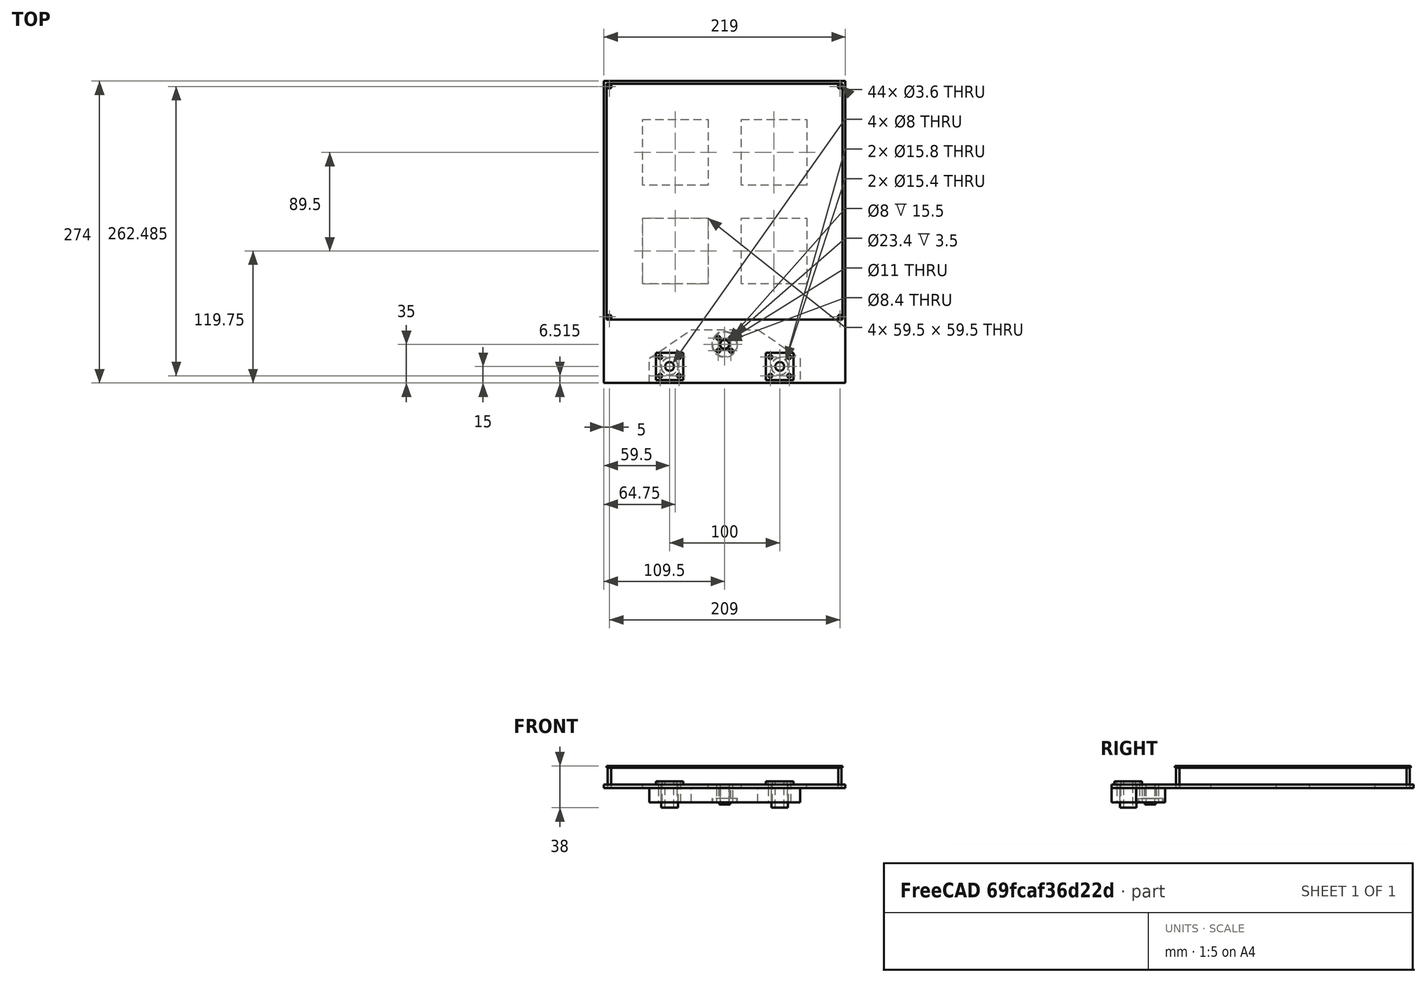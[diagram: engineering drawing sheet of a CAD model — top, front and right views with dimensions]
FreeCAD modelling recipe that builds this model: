
FCSTD DOCUMENT  (FreeCAD 0.16R6706 (Git))
Label: Montagem Mesa
License: All rights reserved
LicenseURL: http://en.wikipedia.org/wiki/All_rights_reserved
objects: Part::FeaturePython×6, Part::Cylinder×4, Part::Compound×1
note: 11 computed .brp shape members not serialized (recipe doc carries the construction recipe); baked Part::Feature solids carry a one-line shape summary decoded from their .brp

FEATURE [Part::FeaturePython] Suporte_Mesa_01  # a2plus imported part (geometry in sourceFile) (typed FeaturePython)
  Placement = pos=(0,-164.5,-18.4) rot=(0,0,1;0rad)
  fixedPosition = true
  sourceFile = <path> Mesa.FCStd
  timeLastImport = 1.50674e+09
  updateColors = true
FEATURE [Part::FeaturePython] Suporte_V_01  # a2plus imported part (geometry in sourceFile) (typed FeaturePython)
  Placement = pos=(0,-129.5,-31.4) rot=(0,0,1;0rad)
  fixedPosition = false
  sourceFile = <path> V.FCStd
  timeLastImport = 1.50665e+09
  updateColors = true
FEATURE [Part::FeaturePython] Castanha_TR8_01  # a2plus imported part (geometry in sourceFile) (typed FeaturePython)
  Placement = pos=(0,-129.5,-31.4) rot=(0,0,1;0rad)
  fixedPosition = false
  sourceFile = <path> TR8.FCStd
  timeLastImport = 1.50665e+09
  updateColors = true
FEATURE [Part::FeaturePython] LMK8UU_01  # a2plus imported part (geometry in sourceFile) (typed FeaturePython)
  Placement = pos=(-50,-149.5,-12.4) rot=(0.707107,0.707106,0;3.14159rad)
  fixedPosition = false
  sourceFile = <path>
  timeLastImport = 1.50665e+09
  updateColors = true
FEATURE [Part::FeaturePython] Mesa_MK1_01  # a2plus imported part (geometry in sourceFile) (typed FeaturePython)
  fixedPosition = false
  sourceFile = <path> MK1.FCStd
  timeLastImport = 1.50665e+09
  updateColors = true
FEATURE [Part::Cylinder] Cylinder  label="Regulador Mesa"
  Angle = 360
  Height = 20
  Placement = pos=(-104.5,104.5,-18.4) rot=(0,0,1;0rad)
  Radius = 1.5
FEATURE [Part::Cylinder] Cylinder001  label="Regulador Mesa001"
  Angle = 360
  Height = 20
  Placement = pos=(104.5,104.5,-18.4) rot=(0,0,1;0rad)
  Radius = 1.5
FEATURE [Part::Cylinder] Cylinder002  label="Regulador Mesa002"
  Angle = 360
  Height = 20
  Placement = pos=(104.5,-104.5,-18.4) rot=(0,0,1;0rad)
  Radius = 1.5
FEATURE [Part::Cylinder] Cylinder003  label="Regulador Mesa003"
  Angle = 360
  Height = 20
  Placement = pos=(-104.5,-104.5,-18.4) rot=(0,0,1;0rad)
  Radius = 1.5
FEATURE [Part::FeaturePython] LMK8UU_002  # a2plus imported part (geometry in sourceFile) (typed FeaturePython)
  Placement = pos=(50,-149.5,-12.4) rot=(0.707107,0.707107,0;3.14159rad)
  fixedPosition = false
  sourceFile = <path>
  timeLastImport = 1.50665e+09
  updateColors = true
FEATURE [Part::Compound] Compound
  Links = -> [LMK8UU_002,Cylinder003,Cylinder002,Cylinder001,Cylinder,Mesa_MK1_01,LMK8UU_01,Castanha_TR8_01,Suporte_V_01,Suporte_Mesa_01]
note: 6 file-system paths scrubbed to <path> (originals preserved in the JSON sidecar)
